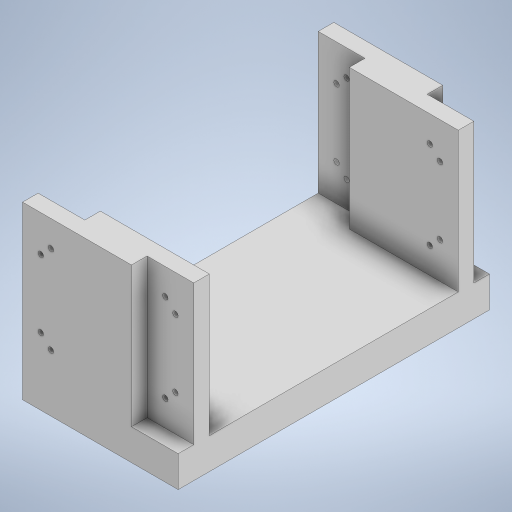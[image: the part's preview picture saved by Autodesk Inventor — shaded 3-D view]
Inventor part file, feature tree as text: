
AUTODESK INVENTOR PART (.ipt)
format: ipt  version: 2023 (Build 270158000, 158)  size: 308,736 bytes
history: native  units: mm
features: sketch x6, extrude x4, hole x2, other x1, mirror x1
ambient origin geometry x8: Origin, YZ Plane, XZ Plane, XY Plane, X Axis, Y Axis, Z Axis, Center Point
bodies: Body1 (feature_tree)
feature tree (14):
  other  "Sólido1"
  extrude  "Extrusión1"  Depth=90.0mm
  hole  "Agujero1"  [1 undecoded]
  extrude  "Extrusión2"  TaperAngle=0.0deg  [1 undecoded]
  extrude  "Extrusión3"  Depth=90.0mm
  hole  "Agujero2"  [1 undecoded]
  extrude  "Extrusión4"  Depth=90.0mm
  mirror  "Simetría1"
  sketch  "Boceto1"  dims[d0=30.0mm d1=90.0mm]
  sketch  "Boceto2"  dims[d2=10.0mm d3=0.0mm]
  sketch  "Boceto3"  dims[d4=1.75mm d5=1.75mm d6=1.75mm d7=1.75mm d8=10.0mm d9=10.0mm d10=10.0mm d11=15.0mm d12=0.0mm]
  sketch  "Boceto4"  dims[d13=30.0mm d14=0.0mm]
  sketch  "Boceto5"  dims[d15=90.0mm d16=15.0mm]
  sketch  "Boceto6"  dims[d17=3.5mm d18=6.0mm d19=4.0mm d20=2.0mm d21=90.0deg d22=8.0mm d23=20.594885mm d24=20.0mm d25=90.0mm d26=40.0mm d27=0.0mm d28=30.0mm d29=0.0mm d30=3.5mm d31=1.75mm d32=1.75mm d33=1.75mm d34=1.75mm d35=10.0mm d36=10.0mm d38=10.0mm d39=10.0mm d40=15.0mm d41=0.0mm d42=15.0mm d43=90.0mm d45=0.0mm d46=3.5mm d47=6.0mm d48=4.0mm d49=2.0mm d50=90.0deg d51=8.0mm d52=20.594885mm d53=20.0mm d54=100.0mm d55=0.0mm]
note: 3 required parameter values undecoded (feature->parameter linkage not recoverable at this tier; creation-order binding heuristic only, values carry confidence <= 0.55)
